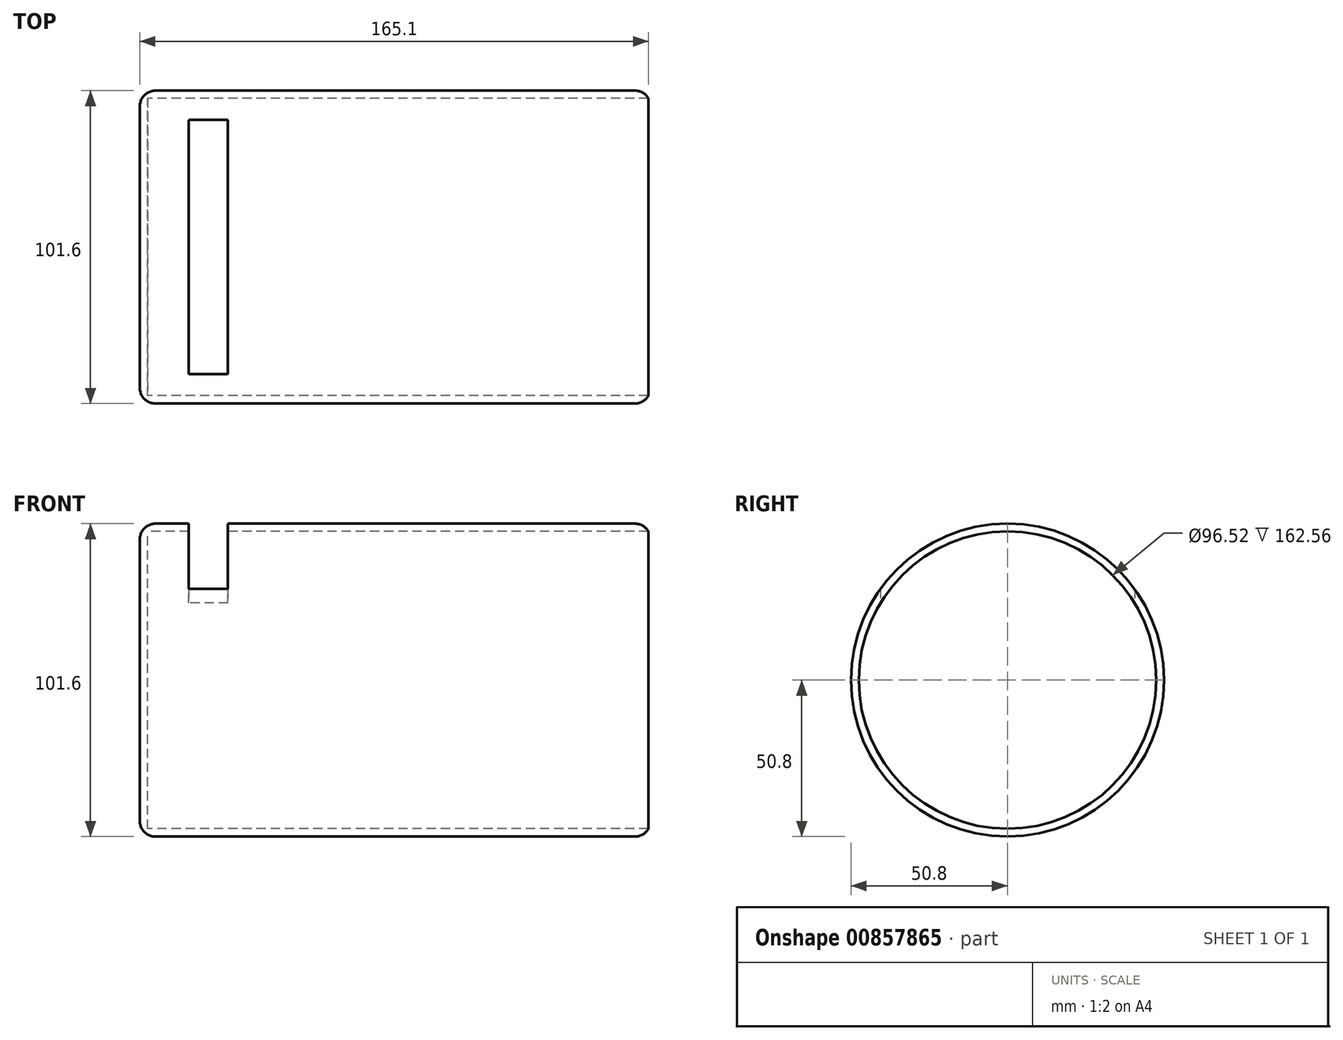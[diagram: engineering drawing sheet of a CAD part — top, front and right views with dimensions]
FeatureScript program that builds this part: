
annotation { "Feature Type Name" : "Feature", "Feature Type Description" : "" }
export const myFeature = defineFeature(function(context is Context, id is Id, definition is map)
    precondition{}
    {
        {
            var Q0;
            Q0=qCreatedBy(makeId("Right.planeOp"),FACE);
            var sketch = newSketch(context, id + "F0", { "sketchPlane" : qUnion([Q0])});
            skCircle(sketch, "E0", {"center": v(0, 0) * mm, "radius": 50.8 * mm});
            skCircle(sketch, "E1.0", {"center": v(0, 0) * mm, "radius": 57.15 * mm});
            skSolve(sketch);
        }
        {
            var Q0;
            Q0=makeQuery(id+"F0.imprint","IMPRINT",FACE,{"disambiguationData":[TD([[makeQuery(id+"F0.imprint","IMPRINT",EDGE,{"derivedFrom":sQuery(id+"F0.wireOp",EDGE,"E0")}),1.0]])]});
            extrude(context, id + "F1", {"entities" : qUnion([Q0]), "endBound" : BoundingType.SYMMETRIC, "depth" : 165.1 * mm, "offsetDistance" : 25.4 * mm});
        }
        {
            var Q0;
            Q0=makeQuery(id+"F1.opExtrude","CAP_FACE",FACE,{"disambiguationData":[OSD([sQuery(id+"F0.wireOp",EDGE,"E0")])],"isStart":false});
            shell(context, id + "F2", {"entities" : qUnion([Q0]), "thickness" : 2.54 * mm});
        }
        {
            var Q0;
            Q0=makeQuery(id+"F1.opExtrude","SWEPT_FACE",FACE,{"disambiguationData":[OSD([sQuery(id+"F0.wireOp",EDGE,"E0")])]});
            fillet(context, id + "F3", {"entities" : qUnion([Q0]), "radius" : 5.08 * mm, "tangentPropagation" : true, "allowEdgeOverflow" : false});
        }
        {
            var Q0;
            Q0=qCreatedBy(makeId("Top.planeOp"),FACE);
            var sketch = newSketch(context, id + "F4", { "sketchPlane" : qUnion([Q0])});
            skLineSegment(sketch, "E2.top", {"start": v(-53.92, 41.28) * mm, "end": v(-66.62, 41.28) * mm});
            skLineSegment(sketch, "E2.left", {"start": v(-53.92, 0) * mm, "end": v(-53.92, 41.28) * mm});
            skLineSegment(sketch, "E2.right", {"start": v(-66.62, 0) * mm, "end": v(-66.62, 41.28) * mm});
            skLineSegment(sketch, "E3.bottom", {"start": v(-53.92, 0) * mm, "end": v(-53.42, 0) * mm});
            skLineSegment(sketch, "E4.top", {"start": v(-66.62, -41.28) * mm, "end": v(-53.92, -41.28) * mm});
            skLineSegment(sketch, "E4.left", {"start": v(-66.62, 0) * mm, "end": v(-66.62, -41.28) * mm});
            skLineSegment(sketch, "E4.right", {"start": v(-53.92, 0) * mm, "end": v(-53.92, -41.28) * mm});
            skSolve(sketch);
        }
        {
            var Q0;
            Q0 = qSketchRegion(id + "F4", true);
            extrude(context, id + "F5", {"entities" : qUnion([Q0]), "operationType" : NewBodyOperationType.REMOVE, "depth" : 152.4 * mm, "offsetDistance" : 25.4 * mm});
        }
    });
